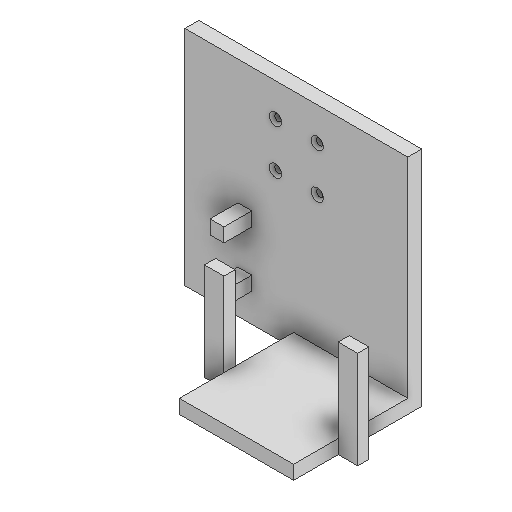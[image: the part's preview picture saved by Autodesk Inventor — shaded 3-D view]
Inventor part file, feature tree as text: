
AUTODESK INVENTOR PART (.ipt)
format: ipt  version: 2025.1 (Build 291241000, 241)  size: 171,520 bytes
history: native  units: mm
features: sketch x6, extrude x5, other x1, hole x1
ambient origin geometry x8: Origin, YZ Plane, XZ Plane, XY Plane, X Axis, Y Axis, Z Axis, Center Point
bodies: Body1 (feature_tree)
feature tree (13):
  other  "Bryła1"
  extrude  "Wyciągnięcie proste1"  Depth=80.0mm
  extrude  "Wyciągnięcie proste2"  Depth=80.0mm
  extrude  "Wyciągnięcie proste3"  Depth=5.0mm TaperAngle=0.0deg
  hole  "Otwór1"  [1 undecoded]
  extrude  "Wyciągnięcie proste4"  Depth=5.0mm
  extrude  "Wyciągnięcie proste5"  Depth=41.0mm TaperAngle=0.0deg
  sketch  "Szkic1"
  sketch  "Szkic2"
  sketch  "Szkic3"
  sketch  "Szkic4"
  sketch  "Szkic5"
  sketch  "Szkic6"
note: 1 required parameter value undecoded (feature->parameter linkage not recoverable at this tier; creation-order binding heuristic only, values carry confidence <= 0.55)
